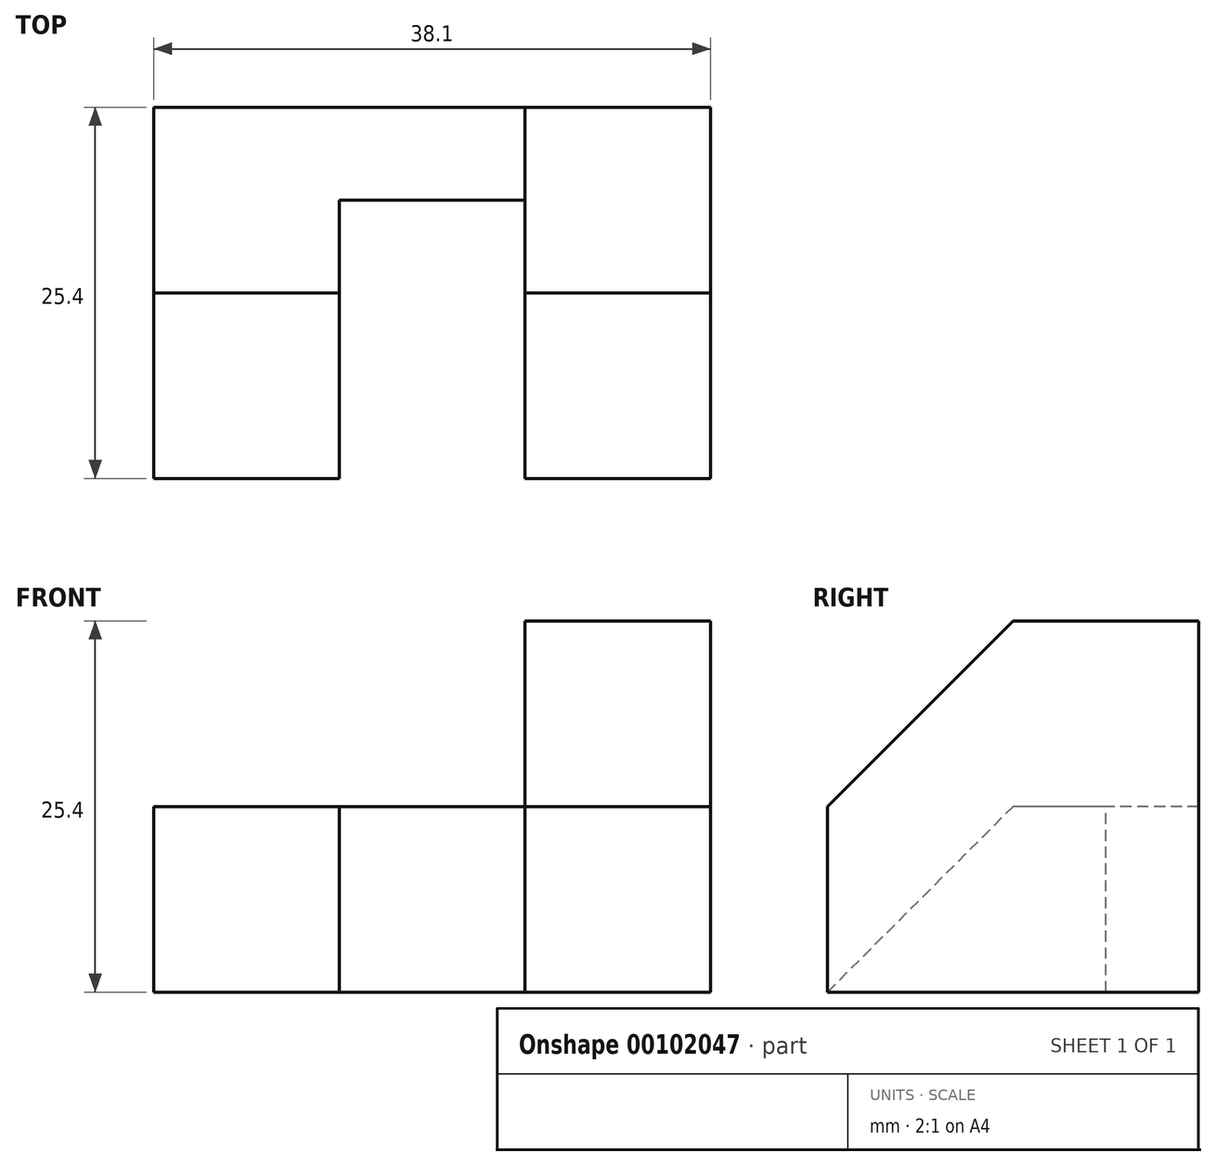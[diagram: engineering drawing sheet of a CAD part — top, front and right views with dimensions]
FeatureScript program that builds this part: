
annotation { "Feature Type Name" : "Feature", "Feature Type Description" : "" }
export const myFeature = defineFeature(function(context is Context, id is Id, definition is map)
    precondition{}
    {
        {
            var Q0;
            Q0=qCreatedBy(makeId("Top.planeOp"),FACE);
            var sketch = newSketch(context, id + "F0", { "sketchPlane" : qUnion([Q0])});
            skLineSegment(sketch, "E0.bottom", {"start": v(0, 0) * mm, "end": v(38.1, 0) * mm});
            skLineSegment(sketch, "E0.top", {"start": v(0, 25.4) * mm, "end": v(38.1, 25.4) * mm});
            skLineSegment(sketch, "E0.left", {"start": v(0, 0) * mm, "end": v(0, 25.4) * mm});
            skLineSegment(sketch, "E0.right", {"start": v(38.1, 0) * mm, "end": v(38.1, 25.4) * mm});
            skSolve(sketch);
        }
        {
            var Q0;
            Q0=makeQuery(id+"F0.imprint","IMPRINT",FACE,{"disambiguationData":[TD([[makeQuery(id+"F0.imprint","IMPRINT",EDGE,{"derivedFrom":sQuery(id+"F0.wireOp",EDGE,"E0.bottom")}),1.0]])]});
            extrude(context, id + "F1", {"entities" : qUnion([Q0]), "depth" : 25.4 * mm});
        }
        {
            var Q0;
            Q0=makeQuery(id+"F1.opExtrude","SWEPT_FACE",FACE,{"disambiguationData":[OSD([sQuery(id+"F0.wireOp",EDGE,"E0.right")])]});
            var sketch = newSketch(context, id + "F2", { "sketchPlane" : qUnion([Q0])});
            skLineSegment(sketch, "E1", {"start": v(0, 25.4) * mm, "end": v(12.7, 25.4) * mm});
            skLineSegment(sketch, "E2", {"start": v(0, 25.4) * mm, "end": v(0, 12.7) * mm});
            skLineSegment(sketch, "E3", {"start": v(12.7, 25.4) * mm, "end": v(0, 12.7) * mm});
            skSolve(sketch);
        }
        {
            var Q0;
            Q0=makeQuery(id+"F2.imprint","IMPRINT",FACE,{"disambiguationData":[TD([[makeQuery(id+"F2.imprint","IMPRINT",EDGE,{"derivedFrom":sQuery(id+"F2.wireOp",EDGE,"E1")}),-1.0]])]});
            extrude(context, id + "F3", {"entities" : qUnion([Q0]), "operationType" : NewBodyOperationType.REMOVE, "oppositeDirection" : true, "depth" : 12.7 * mm});
        }
        {
            var Q0;
            Q0=makeQuery(id+"F1.opExtrude","CAP_FACE",FACE,{"disambiguationData":[OSD([sQuery(id+"F0.wireOp",EDGE,"E0.bottom"),sQuery(id+"F0.wireOp",EDGE,"E0.top"),sQuery(id+"F0.wireOp",EDGE,"E0.left"),sQuery(id+"F0.wireOp",EDGE,"E0.right")])],"isStart":false});
            var sketch = newSketch(context, id + "F4", { "sketchPlane" : qUnion([Q0])});
            skLineSegment(sketch, "E4", {"start": v(25.4, 0) * mm, "end": v(12.7, 0) * mm});
            skLineSegment(sketch, "E5", {"start": v(12.7, 0) * mm, "end": v(12.7, 19.05) * mm});
            skLineSegment(sketch, "E6", {"start": v(12.7, 19.05) * mm, "end": v(25.4, 19.05) * mm});
            skLineSegment(sketch, "E7", {"start": v(25.4, 19.05) * mm, "end": v(25.4, 0) * mm});
            skSolve(sketch);
        }
        {
            var Q0;
            {var subQ1=sQuery(id+"F4.wireOp",EDGE,"E4");Q0=makeQuery(id+"F4.imprint","IMPRINT",FACE,{"disambiguationData":[TD([[makeQuery(id+"F4.imprint","IMPRINT",EDGE,{"derivedFrom":subQ1}),1.0]])]});}
            extrude(context, id + "F5", {"entities" : qUnion([Q0]), "operationType" : NewBodyOperationType.REMOVE, "oppositeDirection" : true, "depth" : 25.4 * mm});
        }
        {
            var Q0;
            {var subQ1=sQuery(id+"F0.wireOp",EDGE,"E0.left");var subQ3=sQuery(id+"F0.wireOp",EDGE,"E0.bottom");Q0=makeQuery(id+"F5.boolean.opBoolean","SPLIT",FACE,{"disambiguationData":[TD([makeQuery(id+"F1.opExtrude","SWEPT_FACE",FACE,{"disambiguationData":[OSD([subQ1])]})])],"derivedFrom":makeQuery(id+"F1.opExtrude","SWEPT_FACE",FACE,{"disambiguationData":[OSD([subQ3])]})});}
            var sketch = newSketch(context, id + "F6", { "sketchPlane" : qUnion([Q0])});
            skLineSegment(sketch, "E8", {"start": v(0, 25.4) * mm, "end": v(0, 12.7) * mm});
            skLineSegment(sketch, "E9", {"start": v(0, 12.7) * mm, "end": v(12.7, 12.7) * mm});
            skLineSegment(sketch, "E10", {"start": v(12.7, 12.7) * mm, "end": v(12.7, 25.4) * mm});
            skLineSegment(sketch, "E11", {"start": v(12.7, 25.4) * mm, "end": v(0, 25.4) * mm});
            skSolve(sketch);
        }
        {
            var Q0;
            Q0=makeQuery(id+"F6.imprint","IMPRINT",FACE,{"disambiguationData":[TD([[makeQuery(id+"F6.imprint","IMPRINT",EDGE,{"derivedFrom":sQuery(id+"F6.wireOp",EDGE,"E8")}),1.0]])]});
            extrude(context, id + "F7", {"entities" : qUnion([Q0]), "operationType" : NewBodyOperationType.REMOVE, "oppositeDirection" : true, "depth" : 25.4 * mm});
        }
        {
            var Q0;
            Q0=makeQuery(id+"F5.boolean.opBoolean","COPY",FACE,{"derivedFrom":makeQuery(id+"F5.opExtrude","SWEPT_FACE",FACE,{"disambiguationData":[OSD([sQuery(id+"F4.wireOp",EDGE,"E6")])]})});
            var sketch = newSketch(context, id + "F8", { "sketchPlane" : qUnion([Q0])});
            skLineSegment(sketch, "E12", {"start": v(12.7, 25.4) * mm, "end": v(12.7, 12.7) * mm});
            skLineSegment(sketch, "E13", {"start": v(12.7, 12.7) * mm, "end": v(25.4, 12.7) * mm});
            skLineSegment(sketch, "E14", {"start": v(25.4, 12.7) * mm, "end": v(25.4, 25.4) * mm});
            skLineSegment(sketch, "E15", {"start": v(25.4, 25.4) * mm, "end": v(12.7, 25.4) * mm});
            skSolve(sketch);
        }
        {
            var Q0;
            Q0=makeQuery(id+"F8.imprint","IMPRINT",FACE,{"disambiguationData":[TD([[makeQuery(id+"F8.imprint","IMPRINT",EDGE,{"derivedFrom":sQuery(id+"F8.wireOp",EDGE,"E12")}),-1.0]])]});
            extrude(context, id + "F9", {"entities" : qUnion([Q0]), "operationType" : NewBodyOperationType.REMOVE, "oppositeDirection" : true, "depth" : 12.7 * mm});
        }
        {
            var Q0;
            Q0=makeQuery(id+"F1.opExtrude","SWEPT_FACE",FACE,{"disambiguationData":[OSD([sQuery(id+"F0.wireOp",EDGE,"E0.left")])]});
            var sketch = newSketch(context, id + "F10", { "sketchPlane" : qUnion([Q0])});
            skLineSegment(sketch, "E16", {"start": v(0, 12.7) * mm, "end": v(-12.7, 12.7) * mm});
            skLineSegment(sketch, "E17", {"start": v(0, 12.7) * mm, "end": v(0, 0) * mm});
            skLineSegment(sketch, "E18", {"start": v(0, 0) * mm, "end": v(-12.7, 12.7) * mm});
            skSolve(sketch);
        }
        {
            var Q0;
            Q0=makeQuery(id+"F10.imprint","IMPRINT",FACE,{"disambiguationData":[TD([[makeQuery(id+"F10.imprint","IMPRINT",EDGE,{"derivedFrom":sQuery(id+"F10.wireOp",EDGE,"E16")}),-1.0]])]});
            extrude(context, id + "F11", {"entities" : qUnion([Q0]), "operationType" : NewBodyOperationType.REMOVE, "oppositeDirection" : true, "depth" : 12.7 * mm});
        }
    });
